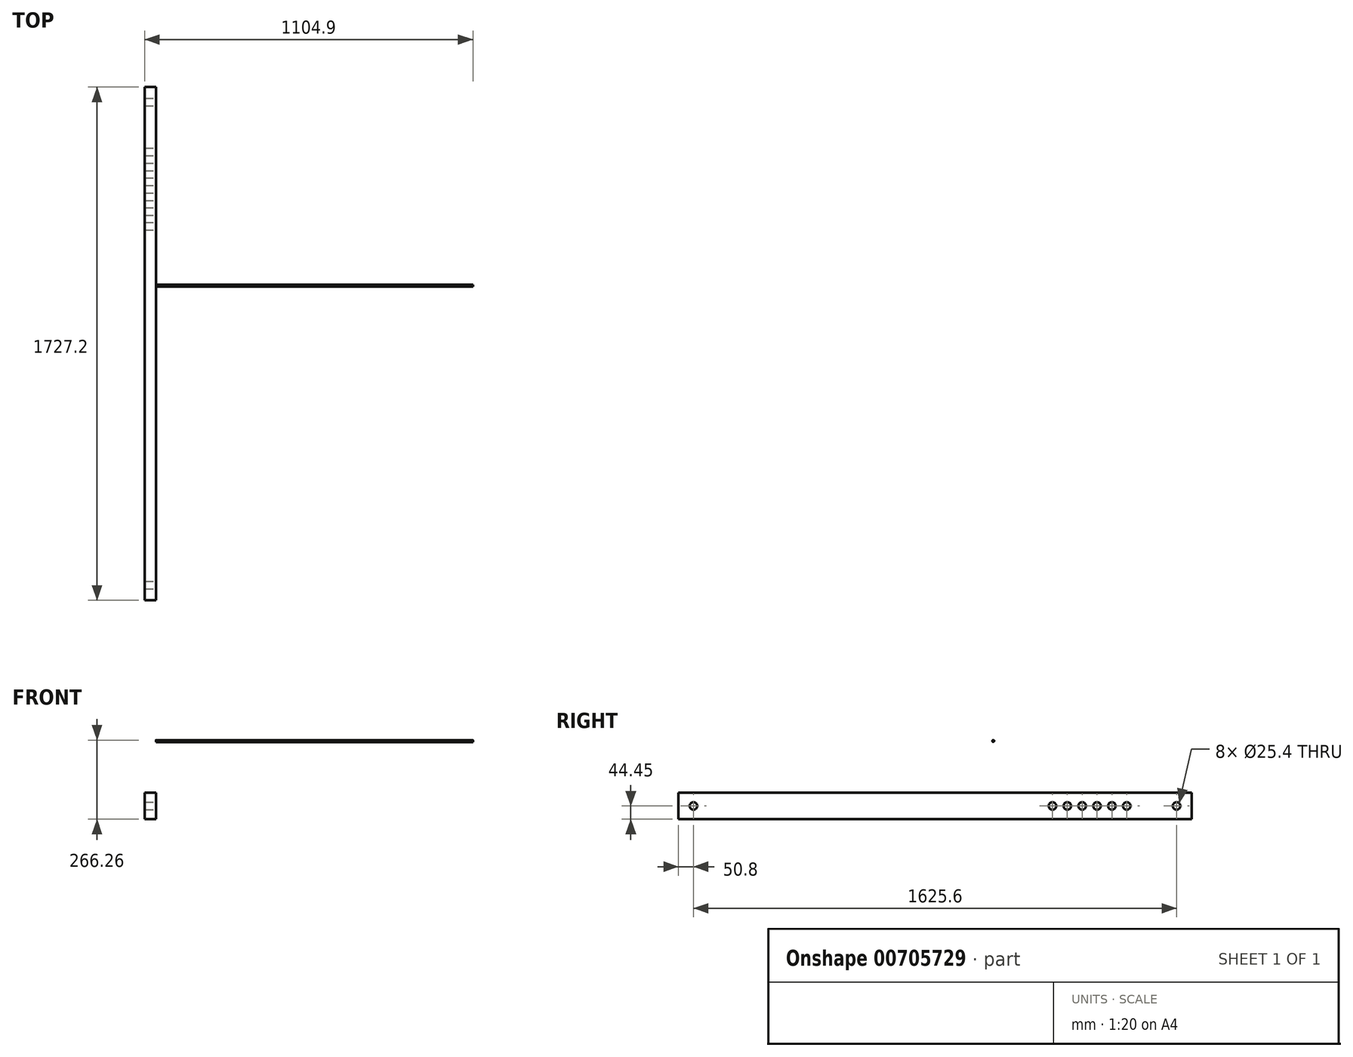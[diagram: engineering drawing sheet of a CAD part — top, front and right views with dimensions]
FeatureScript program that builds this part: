
annotation { "Feature Type Name" : "Feature", "Feature Type Description" : "" }
export const myFeature = defineFeature(function(context is Context, id is Id, definition is map)
    precondition{}
    {
        {
            var Q0;
            Q0=qCreatedBy(makeId("Front.planeOp"),FACE);
            var sketch = newSketch(context, id + "F0", { "sketchPlane" : qUnion([Q0])});
            skLineSegment(sketch, "E0.bottom", {"start": v(19.05, -44.45) * mm, "end": v(-19.05, -44.45) * mm});
            skLineSegment(sketch, "E0.top", {"start": v(19.05, 44.45) * mm, "end": v(-19.05, 44.45) * mm});
            skLineSegment(sketch, "E0.left", {"start": v(19.05, -44.45) * mm, "end": v(19.05, 44.45) * mm});
            skLineSegment(sketch, "E0.right", {"start": v(-19.05, -44.45) * mm, "end": v(-19.05, 44.45) * mm});
            skPoint(sketch, "E0.middle", {"position": v(0, 0) * mm});
            skSolve(sketch);
        }
        {
            var Q0;
            Q0=makeQuery(id+"F0.imprint","IMPRINT",FACE,{"disambiguationData":[TD([[makeQuery(id+"F0.imprint","IMPRINT",EDGE,{"derivedFrom":sQuery(id+"F0.wireOp",EDGE,"E0.bottom")}),-1.0]])]});
            extrude(context, id + "F1", {"entities" : qUnion([Q0]), "depth" : 1727.2 * mm, "offsetDistance" : 25.4 * mm});
        }
        {
            var Q0;
            Q0=makeQuery(id+"F1.opExtrude","SWEPT_FACE",FACE,{"disambiguationData":[OSD([sQuery(id+"F0.wireOp",EDGE,"E0.left")])]});
            var sketch = newSketch(context, id + "F2", { "sketchPlane" : qUnion([Q0])});
            skPoint(sketch, "E1", {"position": v(-468.42, 0) * mm});
            skPoint(sketch, "E2.1.0.0", {"position": v(-418.42, 0) * mm});
            skPoint(sketch, "E2.2.0.0", {"position": v(-368.42, 0) * mm});
            skLineSegment(sketch, "E2.direction1", {"start": v(-468.42, 0) * mm, "end": v(-418.42, 0) * mm, "construction": true});
            skPoint(sketch, "E3.0.3.0", {"position": v(-318.42, 0) * mm});
            skPoint(sketch, "E4", {"position": v(-1676.4, 0) * mm});
            skPoint(sketch, "E5", {"position": v(-50.8, 0) * mm});
            skPoint(sketch, "E6.0.4.0", {"position": v(-268.42, 0) * mm});
            skPoint(sketch, "E6.0.5.0", {"position": v(-218.42, 0) * mm});
            skSolve(sketch);
        }
        {
            var Q0;
            Q0=sQuery(id+"F2.wireOp",VERTEX,"E1");
            var Q1;
            Q1=sQuery(id+"F2.wireOp",VERTEX,"E2.1.0.0");
            var Q2;
            Q2=sQuery(id+"F2.wireOp",VERTEX,"E2.2.0.0");
            var Q3;
            Q3=sQuery(id+"F2.wireOp",VERTEX,"E3.0.3.0");
            var Q4;
            Q4=sQuery(id+"F2.wireOp",VERTEX,"E3.0.4.0");
            var Q5;
            Q5=sQuery(id+"F2.wireOp",VERTEX,"e5ffd7d0-9594-471a-8f72-af7d7aa0a451.0.5.0");
            var Q6;
            Q6=sQuery(id+"F2.wireOp",VERTEX,"E5");
            var Q7;
            Q7=sQuery(id+"F2.wireOp",VERTEX,"E4");
            var Q8;
            Q8=sQuery(id+"F2.wireOp",VERTEX,"E6.0.4.0");
            var Q9;
            Q9=sQuery(id+"F2.wireOp",VERTEX,"E6.0.5.0");
            var Q10;
            Q10=makeQuery(id+"F1.opExtrude","SWEPT_BODY",BODY,{"disambiguationData":[OSD([sQuery(id+"F0.wireOp",EDGE,"E0.bottom"),sQuery(id+"F0.wireOp",EDGE,"E0.top"),sQuery(id+"F0.wireOp",EDGE,"E0.left"),sQuery(id+"F0.wireOp",EDGE,"E0.right")])]});
            hole(context, id + "F3", {"style" : HoleStyle.SIMPLE, "endStyle" : HoleEndStyle.THROUGH, "standardTappedOrClearance" : lookupTablePath({ "standard" : "ANSI", "size" : "1 (1)", "type" : "Drilled" }), "standardBlindInLast" : lookupTablePath({ "standard" : "ANSI", "size" : "1", "type" : "Drilled" }), "holeDiameter" : 25.4 * mm, "majorDiameter" : 6.35 * mm, "isTappedThrough" : true, "tappedDepth" : 12.7 * mm, "tapClearance" : 3, "locations" : qUnion([Q0, Q1, Q2, Q3, Q4, Q5, Q6, Q7, Q8, Q9]), "scope" : qUnion([Q10])});
        }
        {
            var Q0;
            {var subQ0=sQuery(id+"F0.wireOp",EDGE,"E0.left");Q0=makeQuery(id+"F2.imprint","IMPRINT",FACE,{"disambiguationData":[TD([[makeQuery(id+"F2.imprint","IMPRINT",EDGE,{"derivedFrom":makeQuery(id+"F1.opExtrude","CAP_EDGE",EDGE,{"disambiguationData":[OSD([subQ0])],"isStart":true})}),1.0]])]});}
            var sketch = newSketch(context, id + "F4", { "sketchPlane" : qUnion([Q0])});
            skCircle(sketch, "E7", {"center": v(-1066.8, 218.63) * mm, "radius": 3.18 * mm});
            skCircle(sketch, "E8", {"center": v(-667.75, 218.63) * mm, "radius": 3.17 * mm});
            skSolve(sketch);
        }
        {
            var Q0;
            Q0=makeQuery(id+"F4.imprint","IMPRINT",FACE,{"disambiguationData":[TD([[makeQuery(id+"F4.imprint","IMPRINT",EDGE,{"derivedFrom":sQuery(id+"F4.wireOp",EDGE,"E7")}),1.0]])]});
            extrude(context, id + "F5", {"entities" : qUnion([Q0]), "oppositeDirection" : true, "depth" : 203.2 * mm, "offsetDistance" : 25.4 * mm});
        }
        {
            var Q0;
            Q0=makeQuery(id+"F4.imprint","IMPRINT",FACE,{"disambiguationData":[TD([[makeQuery(id+"F4.imprint","IMPRINT",EDGE,{"derivedFrom":sQuery(id+"F4.wireOp",EDGE,"E8")}),1.0]])]});
            extrude(context, id + "F6", {"entities" : qUnion([Q0]), "depth" : 1066.8 * mm, "offsetDistance" : 25.4 * mm});
        }
        {
            var Q0;
            Q0=makeQuery(id+"F5.opExtrude","SWEPT_BODY",BODY,{"disambiguationData":[OSD([sQuery(id+"F4.wireOp",EDGE,"E7")])]});
            deleteBodies(context, id + "F7", {"entities" : qUnion([Q0])});
        }
    });
